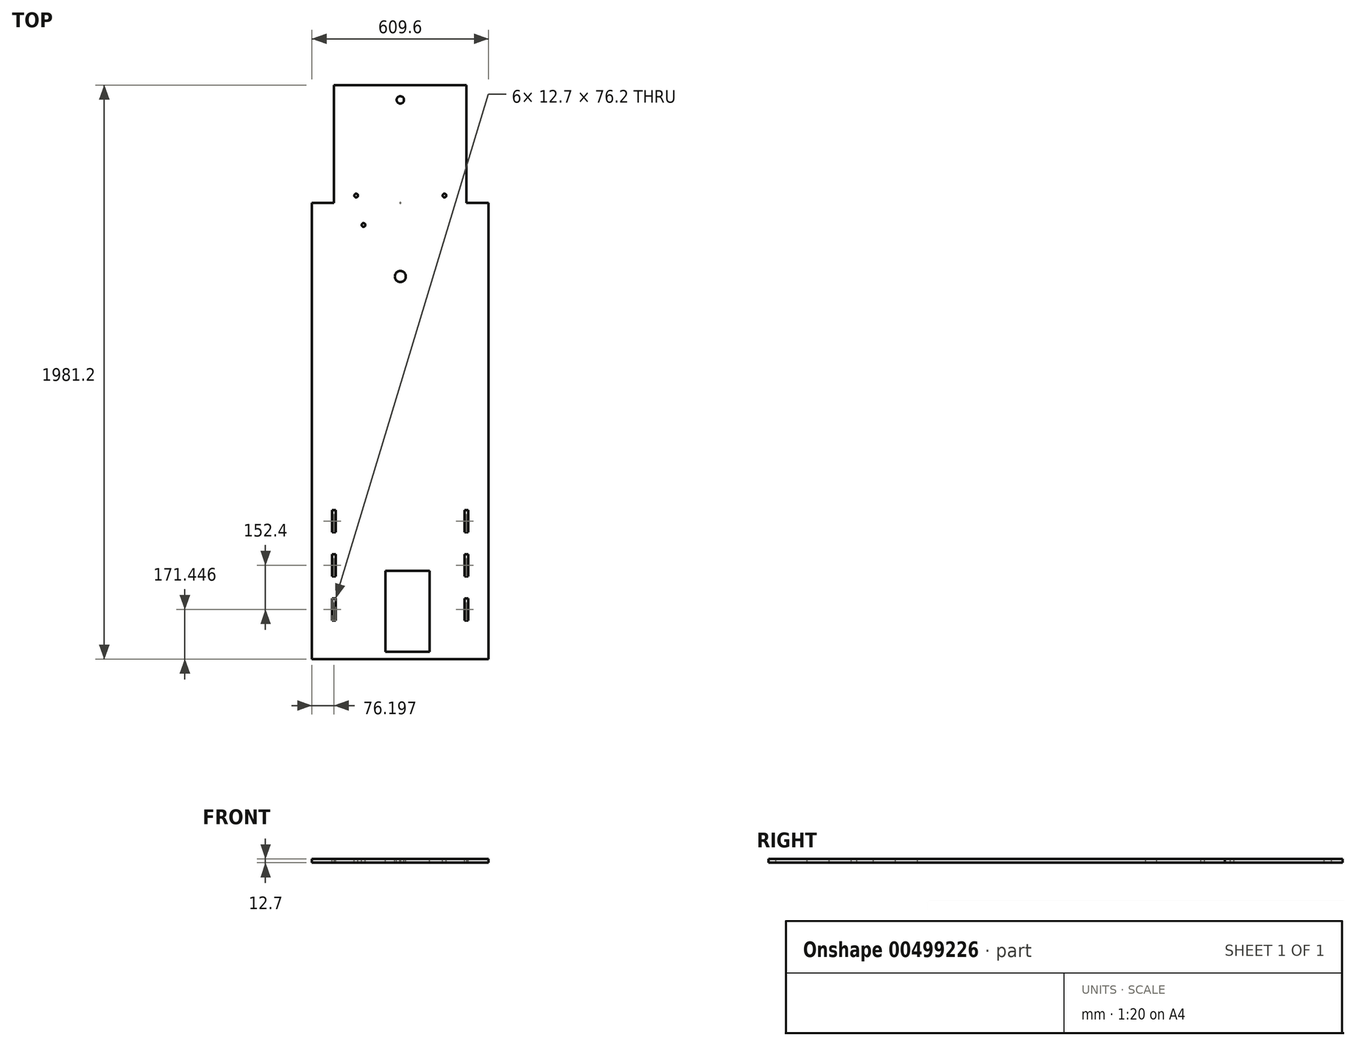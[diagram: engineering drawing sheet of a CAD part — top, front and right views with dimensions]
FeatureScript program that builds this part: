
annotation { "Feature Type Name" : "Feature", "Feature Type Description" : "" }
export const myFeature = defineFeature(function(context is Context, id is Id, definition is map)
    precondition{}
    {
        {
            var Q0;
            Q0=qCreatedBy(makeId("Top.planeOp"),FACE);
            var sketch = newSketch(context, id + "F0", { "sketchPlane" : qUnion([Q0])});
            skLineSegment(sketch, "E0.bottom", {"start": v(-153.04, 1142.62) * mm, "end": v(304.16, 1142.62) * mm});
            skLineSegment(sketch, "E1", {"start": v(-153.04, 1142.62) * mm, "end": v(0, 1142.62) * mm, "construction": true});
            skLineSegment(sketch, "E2.MirrorCS", {"start": v(-67.87, -825.75) * mm, "end": v(-63.8, -838.58) * mm});
            skLineSegment(sketch, "E3", {"start": v(-229.24, 736.22) * mm, "end": v(-229.24, -838.58) * mm});
            skLineSegment(sketch, "E4", {"start": v(-229.24, -838.58) * mm, "end": v(380.36, -838.58) * mm});
            skLineSegment(sketch, "E5.0", {"start": v(304.16, 1142.62) * mm, "end": v(304.16, 736.22) * mm});
            skLineSegment(sketch, "E6", {"start": v(-153.04, 1142.62) * mm, "end": v(-153.04, 736.22) * mm});
            skLineSegment(sketch, "E7", {"start": v(-153.04, 736.22) * mm, "end": v(-229.24, 736.22) * mm});
            skLineSegment(sketch, "E8.MirrorCS", {"start": v(304.16, 736.22) * mm, "end": v(380.36, 736.22) * mm});
            skPoint(sketch, "E9.MirrorCS.end.orphan", {"position": v(304.16, 736.22) * mm});
            skPoint(sketch, "E9.MirrorCS.start.orphan", {"position": v(304.16, 1142.62) * mm});
            skPoint(sketch, "E10.orphan", {"position": v(-229.24, 1142.62) * mm});
            skPoint(sketch, "E0.right.start.orphan", {"position": v(380.36, 1142.62) * mm});
            skLineSegment(sketch, "E11", {"start": v(380.36, 736.22) * mm, "end": v(380.36, -838.58) * mm});
            skPoint(sketch, "E12.start.orphan", {"position": v(75.56, 1142.62) * mm});
            skLineSegment(sketch, "E13", {"start": v(75.56, 1142.62) * mm, "end": v(75.56, -838.58) * mm, "construction": true});
            skSolve(sketch);
        }
        {
            var Q0;
            {var subQ3=sQuery(id+"F0.wireOp",EDGE,"E3");Q0=makeQuery(id+"F0.imprint","IMPRINT",FACE,{"disambiguationData":[TD([[makeQuery(id+"F0.imprint","IMPRINT",EDGE,{"derivedFrom":subQ3}),1.0]])]});}
            extrude(context, id + "F1", {"entities" : qUnion([Q0]), "depth" : 12.7 * mm, "offsetDistance" : 25.4 * mm});
        }
        {
            var Q0;
            Q0=makeQuery(id+"F1.opExtrude","CAP_FACE",FACE,{"disambiguationData":[OSD([sQuery(id+"F0.wireOp",EDGE,"E0.bottom"),sQuery(id+"F0.wireOp",EDGE,"E0.right"),sQuery(id+"F0.wireOp",EDGE,"cz1OnjEI-BDNs-o1tZ-h10i-E5FD8nW2vjBL"),sQuery(id+"F0.wireOp",EDGE,"E3"),sQuery(id+"F0.wireOp",EDGE,"E4")])],"isStart":false});
            var sketch = newSketch(context, id + "F2", { "sketchPlane" : qUnion([Q0])});
            skLineSegment(sketch, "E14", {"start": v(75.56, -838.58) * mm, "end": v(75.56, -813.18) * mm, "construction": true});
            skLineSegment(sketch, "E15", {"start": v(75.56, -813.18) * mm, "end": v(83.38, -813.18) * mm, "construction": true});
            skLineSegment(sketch, "E16", {"start": v(83.38, -813.18) * mm, "end": v(83.38, -787.78) * mm, "construction": true});
            skLineSegment(sketch, "E17", {"start": v(75.56, -813.18) * mm, "end": v(75.56, -533.78) * mm, "construction": true});
            skLineSegment(sketch, "E18.bottom", {"start": v(126.36, -533.78) * mm, "end": v(24.76, -533.78) * mm});
            skLineSegment(sketch, "E18.top", {"start": v(126.36, -813.18) * mm, "end": v(24.76, -813.18) * mm});
            skLineSegment(sketch, "E18.right", {"start": v(24.76, -533.78) * mm, "end": v(24.76, -813.18) * mm});
            skPoint(sketch, "E18.middle", {"position": v(75.56, -673.48) * mm});
            skPoint(sketch, "E19", {"position": v(75.56, 1091.82) * mm});
            skCircle(sketch, "E20", {"center": v(75.56, 1091.82) * mm, "radius": 12.7 * mm});
            skLineSegment(sketch, "E21", {"start": v(75.56, 1091.82) * mm, "end": v(304.16, 1091.82) * mm, "construction": true});
            skLineSegment(sketch, "E22", {"start": v(75.56, 1091.82) * mm, "end": v(-153.04, 1091.82) * mm, "construction": true});
            skLineSegment(sketch, "E23", {"start": v(75.56, 1142.62) * mm, "end": v(75.56, 1091.82) * mm, "construction": true});
            skLineSegment(sketch, "E24", {"start": v(24.76, -533.78) * mm, "end": v(-229.24, -533.78) * mm, "construction": true});
            skLineSegment(sketch, "E25.bottom", {"start": v(24.76, -533.78) * mm, "end": v(177.16, -533.78) * mm});
            skLineSegment(sketch, "E25.top", {"start": v(24.76, -813.18) * mm, "end": v(177.16, -813.18) * mm});
            skLineSegment(sketch, "E25.right", {"start": v(177.16, -533.78) * mm, "end": v(177.16, -813.18) * mm});
            skSolve(sketch);
        }
        {
            var Q0;
            Q0 = qSketchRegion(id + "F2", true);
            extrude(context, id + "F3", {"entities" : qUnion([Q0]), "operationType" : NewBodyOperationType.REMOVE, "oppositeDirection" : true, "depth" : 19.05 * mm, "offsetDistance" : 25.4 * mm});
        }
        {
            var Q0;
            Q0=makeQuery(id+"F1.opExtrude","CAP_FACE",FACE,{"disambiguationData":[OSD([sQuery(id+"F0.wireOp",EDGE,"E3"),sQuery(id+"F0.wireOp",EDGE,"E4"),sQuery(id+"F0.wireOp",EDGE,"E0.bottom"),sQuery(id+"F0.wireOp",EDGE,"E5.0"),sQuery(id+"F0.wireOp",EDGE,"E6"),sQuery(id+"F0.wireOp",EDGE,"E7"),sQuery(id+"F0.wireOp",EDGE,"E8.MirrorCS"),sQuery(id+"F0.wireOp",EDGE,"E11")])],"isStart":false});
            var sketch = newSketch(context, id + "F4", { "sketchPlane" : qUnion([Q0])});
            skLineSegment(sketch, "E26.0", {"start": v(-153.04, 583.82) * mm, "end": v(-229.24, 583.82) * mm, "construction": true});
            skLineSegment(sketch, "E27", {"start": v(-229.24, 583.82) * mm, "end": v(-153.04, 583.82) * mm, "construction": true});
            skPoint(sketch, "E27.endSnap0", {"position": v(-191.14, 583.82) * mm});
            skPoint(sketch, "E28", {"position": v(-51.44, 583.82) * mm});
            skLineSegment(sketch, "E29.0", {"start": v(304.16, 812.42) * mm, "end": v(151.76, 812.42) * mm, "construction": true});
            skPoint(sketch, "E30", {"position": v(227.96, 812.42) * mm});
            skLineSegment(sketch, "E31", {"start": v(-153.04, -743.33) * mm, "end": v(-153.04, -286.13) * mm, "construction": true});
            skLineSegment(sketch, "E32", {"start": v(24.76, -813.18) * mm, "end": v(24.76, -743.33) * mm});
            skLineSegment(sketch, "E33", {"start": v(-153.04, -286.13) * mm, "end": v(304.16, -286.13) * mm, "construction": true});
            skLineSegment(sketch, "E34", {"start": v(304.16, -286.13) * mm, "end": v(304.16, -743.33) * mm, "construction": true});
            skLineSegment(sketch, "E35", {"start": v(304.16, -743.33) * mm, "end": v(-153.04, -743.33) * mm, "construction": true});
            skPoint(sketch, "E36", {"position": v(75.56, -286.13) * mm});
            skPoint(sketch, "E37", {"position": v(75.56, -838.58) * mm});
            skPoint(sketch, "E38", {"position": v(75.56, -813.18) * mm});
            skLineSegment(sketch, "E39.bottom", {"start": v(-159.4, -705.23) * mm, "end": v(-146.7, -705.23) * mm});
            skLineSegment(sketch, "E39.top", {"start": v(-159.4, -629.03) * mm, "end": v(-146.7, -629.03) * mm});
            skLineSegment(sketch, "E39.left", {"start": v(-159.4, -705.23) * mm, "end": v(-159.4, -629.03) * mm});
            skLineSegment(sketch, "E39.right", {"start": v(-146.7, -705.23) * mm, "end": v(-146.7, -629.03) * mm});
            skPoint(sketch, "E40", {"position": v(-153.04, -705.23) * mm});
            skLineSegment(sketch, "E41.bottom", {"start": v(-159.4, -552.83) * mm, "end": v(-146.7, -552.83) * mm});
            skLineSegment(sketch, "E41.top", {"start": v(-159.4, -476.63) * mm, "end": v(-146.7, -476.63) * mm});
            skLineSegment(sketch, "E41.left", {"start": v(-159.4, -552.83) * mm, "end": v(-159.4, -476.63) * mm});
            skLineSegment(sketch, "E41.right", {"start": v(-146.7, -552.83) * mm, "end": v(-146.7, -476.63) * mm});
            skPoint(sketch, "E42", {"position": v(-153.04, -552.83) * mm});
            skLineSegment(sketch, "E43.bottom", {"start": v(-159.4, -400.43) * mm, "end": v(-146.7, -400.43) * mm});
            skLineSegment(sketch, "E43.top", {"start": v(-159.4, -324.23) * mm, "end": v(-146.7, -324.23) * mm});
            skLineSegment(sketch, "E43.left", {"start": v(-159.4, -400.43) * mm, "end": v(-159.4, -324.23) * mm});
            skLineSegment(sketch, "E43.right", {"start": v(-146.7, -400.43) * mm, "end": v(-146.7, -324.23) * mm});
            skPoint(sketch, "E44", {"position": v(-153.04, -400.43) * mm});
            skLineSegment(sketch, "E45", {"start": v(-153.04, -743.33) * mm, "end": v(-153.04, -705.23) * mm, "construction": true});
            skLineSegment(sketch, "E46", {"start": v(-153.04, -324.23) * mm, "end": v(-153.04, -286.13) * mm, "construction": true});
            skLineSegment(sketch, "E47", {"start": v(-153.04, -286.13) * mm, "end": v(-153.04, -324.23) * mm, "construction": true});
            skLineSegment(sketch, "E48", {"start": v(-153.04, -629.03) * mm, "end": v(-153.04, -552.83) * mm, "construction": true});
            skLineSegment(sketch, "E49", {"start": v(75.56, -286.13) * mm, "end": v(75.56, -480.5) * mm, "construction": true});
            skLineSegment(sketch, "E50.MirrorCS", {"start": v(310.5, -552.83) * mm, "end": v(310.5, -476.63) * mm});
            skLineSegment(sketch, "E51.MirrorCS", {"start": v(310.5, -476.63) * mm, "end": v(297.8, -476.63) * mm});
            skLineSegment(sketch, "E52.MirrorCS", {"start": v(297.8, -552.83) * mm, "end": v(297.8, -476.63) * mm});
            skLineSegment(sketch, "E53.MirrorCS", {"start": v(310.5, -552.83) * mm, "end": v(297.8, -552.83) * mm});
            skLineSegment(sketch, "E54.MirrorCS", {"start": v(310.5, -629.03) * mm, "end": v(297.8, -629.03) * mm});
            skLineSegment(sketch, "E55.MirrorCS", {"start": v(310.5, -705.23) * mm, "end": v(310.5, -629.03) * mm});
            skLineSegment(sketch, "E56.MirrorCS", {"start": v(297.8, -705.23) * mm, "end": v(297.8, -629.03) * mm});
            skLineSegment(sketch, "E57.MirrorCS", {"start": v(310.5, -705.23) * mm, "end": v(297.8, -705.23) * mm});
            skLineSegment(sketch, "E58.MirrorCS", {"start": v(310.5, -400.43) * mm, "end": v(310.5, -324.23) * mm});
            skLineSegment(sketch, "E59.MirrorCS", {"start": v(310.5, -400.43) * mm, "end": v(297.8, -400.43) * mm});
            skLineSegment(sketch, "E60.MirrorCS", {"start": v(297.8, -400.43) * mm, "end": v(297.8, -324.23) * mm});
            skLineSegment(sketch, "E61.MirrorCS", {"start": v(310.5, -324.23) * mm, "end": v(297.8, -324.23) * mm});
            skLineSegment(sketch, "E62", {"start": v(227.96, 812.42) * mm, "end": v(227.96, 761.62) * mm, "construction": true});
            skCircle(sketch, "E63", {"center": v(227.96, 761.62) * mm, "radius": 6.35 * mm});
            skCircle(sketch, "E64", {"center": v(-76.84, 761.62) * mm, "radius": 6.35 * mm});
            skLineSegment(sketch, "E65", {"start": v(297.8, -324.23) * mm, "end": v(-146.7, -324.23) * mm, "construction": true});
            skLineSegment(sketch, "E66.0", {"start": v(227.96, 736.22) * mm, "end": v(304.16, 736.22) * mm});
            skPoint(sketch, "E67", {"position": v(75.56, 736.22) * mm});
            skPoint(sketch, "E68.orphan", {"position": v(-153.04, 736.22) * mm});
            skPoint(sketch, "E69.start.orphan", {"position": v(75.56, 1142.62) * mm});
            skCircle(sketch, "E70", {"center": v(75.56, 736.22) * mm, "radius": 1.59 * mm});
            skLineSegment(sketch, "E71", {"start": v(-229.24, 621.92) * mm, "end": v(75.56, 621.92) * mm, "construction": true});
            skLineSegment(sketch, "E72", {"start": v(75.56, 545.72) * mm, "end": v(-381.64, 545.72) * mm, "construction": true});
            skLineSegment(sketch, "E73", {"start": v(-381.64, 545.72) * mm, "end": v(-381.64, 621.92) * mm, "construction": true});
            skLineSegment(sketch, "E74", {"start": v(-381.64, 621.92) * mm, "end": v(-229.24, 621.92) * mm, "construction": true});
            skLineSegment(sketch, "E75", {"start": v(37.46, 545.72) * mm, "end": v(113.66, 545.72) * mm, "construction": true});
            skPoint(sketch, "E76", {"position": v(75.56, 545.72) * mm});
            skLineSegment(sketch, "E77", {"start": v(113.66, 545.72) * mm, "end": v(113.66, 621.92) * mm, "construction": true});
            skLineSegment(sketch, "E78", {"start": v(113.66, 621.92) * mm, "end": v(75.56, 621.92) * mm, "construction": true});
            skPoint(sketch, "E79.orphan", {"position": v(-51.44, 621.92) * mm});
            skPoint(sketch, "E80.orphan", {"position": v(-51.44, 545.72) * mm});
            skLineSegment(sketch, "E81.bottom", {"start": v(113.66, 545.72) * mm, "end": v(37.46, 545.72) * mm, "construction": true});
            skLineSegment(sketch, "E81.top", {"start": v(113.66, -552.83) * mm, "end": v(37.46, -552.83) * mm, "construction": true});
            skLineSegment(sketch, "E81.left", {"start": v(113.66, 545.72) * mm, "end": v(113.66, -552.83) * mm, "construction": true});
            skLineSegment(sketch, "E81.right", {"start": v(37.46, 545.72) * mm, "end": v(37.46, -552.83) * mm, "construction": true});
            skLineSegment(sketch, "E82", {"start": v(310.5, -324.23) * mm, "end": v(310.5, 736.22) * mm, "construction": true});
            skLineSegment(sketch, "E83", {"start": v(342.26, 736.22) * mm, "end": v(342.26, 206) * mm, "construction": true});
            skLineSegment(sketch, "E84", {"start": v(380.36, 206) * mm, "end": v(75.56, 206) * mm, "construction": true});
            skPoint(sketch, "E85", {"position": v(75.56, 206) * mm});
            skLineSegment(sketch, "E86", {"start": v(75.56, 206) * mm, "end": v(75.56, 307.6) * mm, "construction": true});
            skLineSegment(sketch, "E87", {"start": v(21.86, 1142.62) * mm, "end": v(21.86, 482.22) * mm, "construction": true});
            skCircle(sketch, "E88", {"center": v(75.56, 482.22) * mm, "radius": 19.05 * mm});
            skLineSegment(sketch, "E89", {"start": v(-51.44, 583.82) * mm, "end": v(-51.44, 660.02) * mm, "construction": true});
            skCircle(sketch, "E90", {"center": v(-51.44, 660.02) * mm, "radius": 6.35 * mm});
            skSolve(sketch);
        }
        {
            var Q0;
            Q0 = qSketchRegion(id + "F4", true);
            extrude(context, id + "F5", {"entities" : qUnion([Q0]), "operationType" : NewBodyOperationType.REMOVE, "oppositeDirection" : true, "depth" : 19.05 * mm, "offsetDistance" : 25.4 * mm});
        }
        {
            var Q0;
            Q0 = qSketchRegion(id + "F4", true);
            extrude(context, id + "F6", {"entities" : qUnion([Q0]), "operationType" : NewBodyOperationType.REMOVE, "oppositeDirection" : true, "depth" : 12.7 * mm, "offsetDistance" : 25.4 * mm});
        }
        {
            var Q0;
            Q0=makeQuery(id+"F1.opExtrude","CAP_FACE",FACE,{"disambiguationData":[OSD([sQuery(id+"F0.wireOp",EDGE,"E3"),sQuery(id+"F0.wireOp",EDGE,"E4"),sQuery(id+"F0.wireOp",EDGE,"E0.bottom"),sQuery(id+"F0.wireOp",EDGE,"E5.0"),sQuery(id+"F0.wireOp",EDGE,"E6"),sQuery(id+"F0.wireOp",EDGE,"E7"),sQuery(id+"F0.wireOp",EDGE,"E8.MirrorCS"),sQuery(id+"F0.wireOp",EDGE,"E11")])],"isStart":false});
            var sketch = newSketch(context, id + "F7", { "sketchPlane" : qUnion([Q0])});
            skCircle(sketch, "E91", {"center": v(75.56, 736.22) * mm, "radius": 1.59 * mm});
            skSolve(sketch);
        }
        {
            var Q0;
            Q0 = qSketchRegion(id + "F7", true);
            extrude(context, id + "F8", {"entities" : qUnion([Q0]), "operationType" : NewBodyOperationType.ADD, "oppositeDirection" : true, "depth" : 3.17 * mm, "offsetDistance" : 25.4 * mm});
        }
    });
